# Revit family: G6 PLR MS400890MX-V2
name_source: partatom
category: Datengeräte
units: mm (PartAtom-declared; Revit-internal decimal feet)

## family parameters
Arbeitsebenenbasiert = Nein
Beim Laden mit Abzugskörper schneiden = Nein
Bemaßung runder Anschluss = Durchmesser verwenden
Beschriftungsausrichtung beibehalten = Nein
Gemeinsam genutzt = Nein
Immer vertikal = Ja
OmniClass-Nummer = 23.85.50.17
OmniClass-Titel = Communication and Data Processing Equipment
Raumberechnungspunkt = Nein
Teiletyp = Normal

## types (1)
- G6 PLR MS400890MX-V2
    Anschluss  7 = 2x I/O
    Anschluss 1 = 8x 100/1000X SFP-Slots - 10/100/1000T (Combo)
    Anschluss 2 = 17x 10/100/1000T
    Anschluss 3 = 16x PoE+
    Anschluss 4 = 1x PD
    Anschluss 5 = 1x USB, SD-Karte inkl
    Anschluss 6 = RS-232 Port (RJ-45)
    Anschluss 7 = 0 mm
    Artikelnummer = MS400890MX-V2
    Ausführung = 19", managed switch
    Beschreibung = 25-Port GbE Industrial PLR Switch 19" PoE+
    Hersteller = MICROSENS
    Material = Edelstahl AISI 304
    Material 2 = Stahl, 43-245
    Spannung Input = 2x 24..57VDC
    Vorgabe-Ansicht = 0 mm
